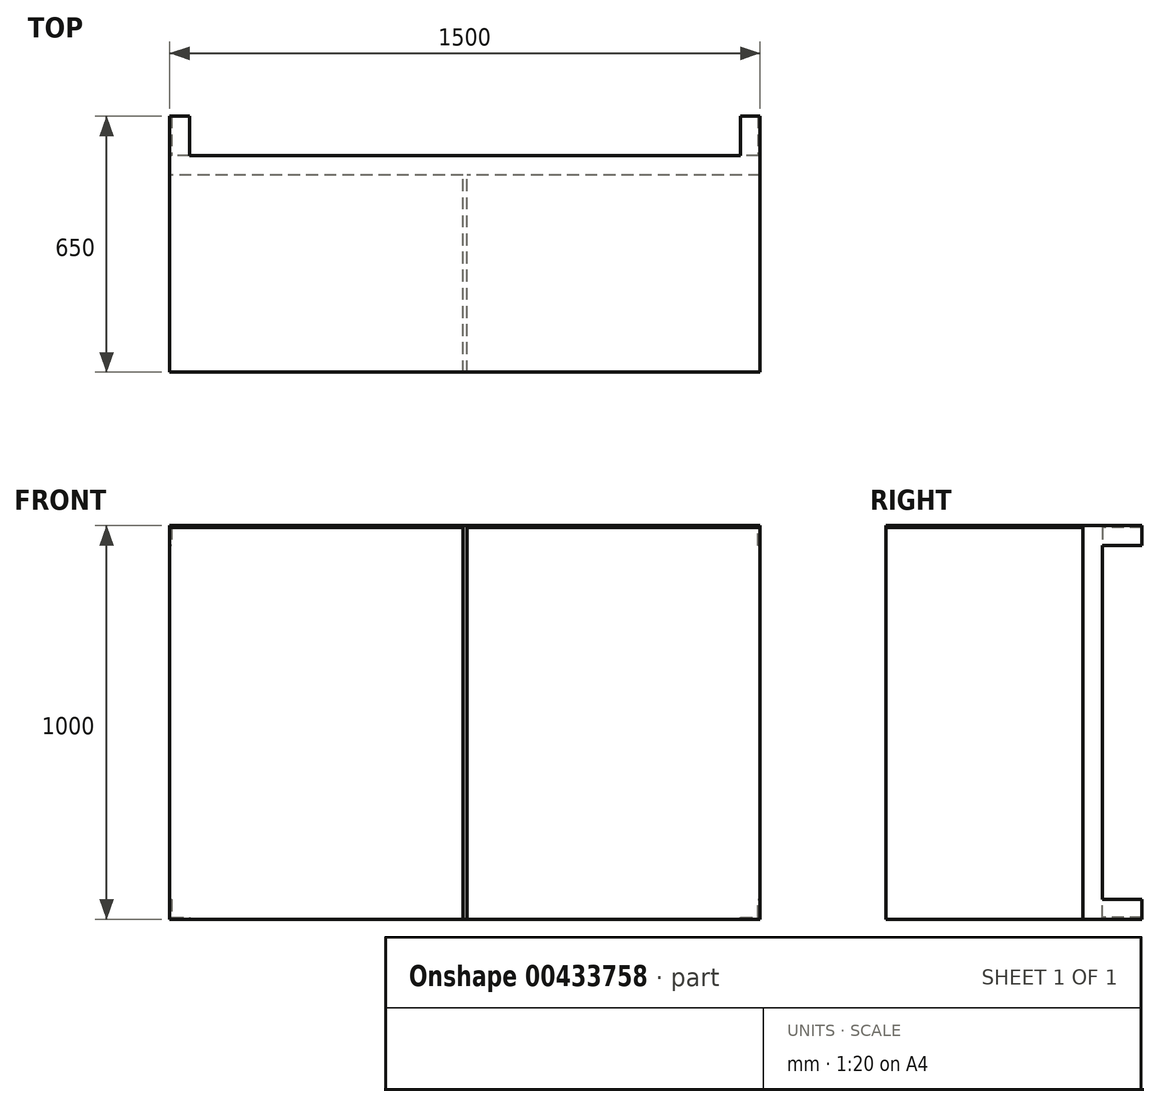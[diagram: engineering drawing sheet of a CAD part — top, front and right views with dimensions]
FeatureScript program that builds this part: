
annotation { "Feature Type Name" : "Feature", "Feature Type Description" : "" }
export const myFeature = defineFeature(function(context is Context, id is Id, definition is map)
    precondition{}
    {
        {
            var Q0;
            Q0=qCreatedBy(makeId("Front.planeOp"),FACE);
            var sketch = newSketch(context, id + "F0", { "sketchPlane" : qUnion([Q0])});
            skLineSegment(sketch, "E0.bottom", {"start": v(750, -500) * mm, "end": v(-750, -500) * mm});
            skLineSegment(sketch, "E0.top", {"start": v(750, 500) * mm, "end": v(-750, 500) * mm});
            skLineSegment(sketch, "E0.left", {"start": v(750, -500) * mm, "end": v(750, 500) * mm});
            skLineSegment(sketch, "E0.right", {"start": v(-750, -500) * mm, "end": v(-750, 500) * mm});
            skPoint(sketch, "E0.middle", {"position": v(0, 0) * mm});
            skSolve(sketch);
        }
        {
            var Q0;
            Q0=makeQuery(id+"F0.imprint","IMPRINT",FACE,{"disambiguationData":[TD([[makeQuery(id+"F0.imprint","IMPRINT",EDGE,{"derivedFrom":sQuery(id+"F0.wireOp",EDGE,"E0.bottom")}),-1.0]])]});
            extrude(context, id + "F1", {"entities" : qUnion([Q0]), "endBound" : BoundingType.SYMMETRIC, "depth" : 50 * mm});
        }
        {
            var Q0;
            Q0=makeQuery(id+"F1.opExtrude","CAP_FACE",FACE,{"disambiguationData":[OSD([sQuery(id+"F0.wireOp",EDGE,"E0.bottom"),sQuery(id+"F0.wireOp",EDGE,"E0.top"),sQuery(id+"F0.wireOp",EDGE,"E0.left"),sQuery(id+"F0.wireOp",EDGE,"E0.right")])],"isStart":true});
            var sketch = newSketch(context, id + "F2", { "sketchPlane" : qUnion([Q0])});
            skLineSegment(sketch, "E1", {"start": v(750, -500) * mm, "end": v(750, -450) * mm});
            skLineSegment(sketch, "E2", {"start": v(750, -500) * mm, "end": v(700, -500) * mm});
            skLineSegment(sketch, "E3", {"start": v(750, -450) * mm, "end": v(745, -450) * mm});
            skLineSegment(sketch, "E4", {"start": v(745, -450) * mm, "end": v(745, -495) * mm});
            skLineSegment(sketch, "E5", {"start": v(745, -495) * mm, "end": v(700, -495) * mm});
            skLineSegment(sketch, "E6", {"start": v(700, -495) * mm, "end": v(700, -500) * mm});
            skLineSegment(sketch, "E7", {"start": v(-750, -500) * mm, "end": v(-700, -500) * mm});
            skLineSegment(sketch, "E8", {"start": v(-750, -500) * mm, "end": v(-750, -450) * mm});
            skLineSegment(sketch, "E9", {"start": v(-700, -500) * mm, "end": v(-700, -495) * mm});
            skLineSegment(sketch, "E10", {"start": v(-700, -495) * mm, "end": v(-745, -495) * mm});
            skLineSegment(sketch, "E11", {"start": v(-745, -495) * mm, "end": v(-745, -450) * mm});
            skLineSegment(sketch, "E12", {"start": v(-745, -450) * mm, "end": v(-750, -450) * mm});
            skLineSegment(sketch, "E13", {"start": v(-750, 500) * mm, "end": v(-750, 450) * mm});
            skLineSegment(sketch, "E14", {"start": v(-750, 500) * mm, "end": v(-700, 500) * mm});
            skLineSegment(sketch, "E15", {"start": v(-750, 450) * mm, "end": v(-745, 450) * mm});
            skLineSegment(sketch, "E16", {"start": v(-745, 450) * mm, "end": v(-745, 495) * mm});
            skLineSegment(sketch, "E17", {"start": v(-745, 495) * mm, "end": v(-700, 495) * mm});
            skLineSegment(sketch, "E18", {"start": v(-700, 495) * mm, "end": v(-700, 500) * mm});
            skLineSegment(sketch, "E19", {"start": v(750, 500) * mm, "end": v(700, 500) * mm});
            skLineSegment(sketch, "E20", {"start": v(750, 500) * mm, "end": v(750, 450) * mm});
            skLineSegment(sketch, "E21", {"start": v(700, 500) * mm, "end": v(700, 495) * mm});
            skLineSegment(sketch, "E22", {"start": v(700, 495) * mm, "end": v(745, 495) * mm});
            skLineSegment(sketch, "E23", {"start": v(745, 495) * mm, "end": v(745, 450) * mm});
            skLineSegment(sketch, "E24", {"start": v(745, 450) * mm, "end": v(750, 450) * mm});
            skSolve(sketch);
        }
        {
            var Q0;
            Q0=makeQuery(id+"F2.imprint","IMPRINT",FACE,{"disambiguationData":[TD([[makeQuery(id+"F2.imprint","IMPRINT",EDGE,{"derivedFrom":sQuery(id+"F2.wireOp",EDGE,"E1")}),1.0]])]});
            var Q1;
            Q1=makeQuery(id+"F2.imprint","IMPRINT",FACE,{"disambiguationData":[TD([[makeQuery(id+"F2.imprint","IMPRINT",EDGE,{"derivedFrom":sQuery(id+"F2.wireOp",EDGE,"E7")}),1.0]])]});
            var Q2;
            Q2=makeQuery(id+"F2.imprint","IMPRINT",FACE,{"disambiguationData":[TD([[makeQuery(id+"F2.imprint","IMPRINT",EDGE,{"derivedFrom":sQuery(id+"F2.wireOp",EDGE,"E13")}),-1.0]])]});
            var Q3;
            Q3=makeQuery(id+"F2.imprint","IMPRINT",FACE,{"disambiguationData":[TD([[makeQuery(id+"F2.imprint","IMPRINT",EDGE,{"derivedFrom":sQuery(id+"F2.wireOp",EDGE,"E19")}),-1.0]])]});
            extrude(context, id + "F3", {"entities" : qUnion([Q0, Q1, Q2, Q3]), "operationType" : NewBodyOperationType.ADD, "depth" : 100 * mm});
        }
        {
            var Q0;
            Q0=makeQuery(id+"F1.opExtrude","CAP_FACE",FACE,{"disambiguationData":[OSD([sQuery(id+"F0.wireOp",EDGE,"E0.bottom"),sQuery(id+"F0.wireOp",EDGE,"E0.top"),sQuery(id+"F0.wireOp",EDGE,"E0.left"),sQuery(id+"F0.wireOp",EDGE,"E0.right")])],"isStart":false});
            var sketch = newSketch(context, id + "F4", { "sketchPlane" : qUnion([Q0])});
            skLineSegment(sketch, "E25.bottom", {"start": v(750, 500) * mm, "end": v(-750, 500) * mm});
            skLineSegment(sketch, "E25.top", {"start": v(750, 495) * mm, "end": v(-750, 495) * mm});
            skLineSegment(sketch, "E25.left", {"start": v(750, 500) * mm, "end": v(750, 495) * mm});
            skLineSegment(sketch, "E25.right", {"start": v(-750, 500) * mm, "end": v(-750, 495) * mm});
            skSolve(sketch);
        }
        {
            var Q0;
            Q0=makeQuery(id+"F4.imprint","IMPRINT",FACE,{"disambiguationData":[TD([[makeQuery(id+"F4.imprint","IMPRINT",EDGE,{"derivedFrom":sQuery(id+"F4.wireOp",EDGE,"E25.bottom")}),1.0]])]});
            extrude(context, id + "F5", {"entities" : qUnion([Q0]), "operationType" : NewBodyOperationType.ADD, "depth" : 500 * mm});
        }
        {
            var Q0;
            Q0=makeQuery(id+"F1.opExtrude","CAP_FACE",FACE,{"disambiguationData":[OSD([sQuery(id+"F0.wireOp",EDGE,"E0.bottom"),sQuery(id+"F0.wireOp",EDGE,"E0.top"),sQuery(id+"F0.wireOp",EDGE,"E0.left"),sQuery(id+"F0.wireOp",EDGE,"E0.right")])],"isStart":false});
            var sketch = newSketch(context, id + "F6", { "sketchPlane" : qUnion([Q0])});
            skLineSegment(sketch, "E26.bottom", {"start": v(0, -500) * mm, "end": v(5, -500) * mm});
            skLineSegment(sketch, "E26.top", {"start": v(0, 495) * mm, "end": v(5, 495) * mm});
            skLineSegment(sketch, "E26.right", {"start": v(5, -500) * mm, "end": v(5, 495) * mm});
            skLineSegment(sketch, "E27.MirrorCS", {"start": v(-5, -500) * mm, "end": v(-5, 495) * mm});
            skLineSegment(sketch, "E28", {"start": v(-5, -500) * mm, "end": v(0, -500) * mm});
            skLineSegment(sketch, "E29", {"start": v(-5, 495) * mm, "end": v(0, 495) * mm});
            skSolve(sketch);
        }
        {
            var Q0;
            Q0=makeQuery(id+"F6.imprint","IMPRINT",FACE,{"disambiguationData":[TD([[makeQuery(id+"F6.imprint","IMPRINT",EDGE,{"derivedFrom":sQuery(id+"F6.wireOp",EDGE,"E26.bottom")}),-1.0]])]});
            extrude(context, id + "F7", {"entities" : qUnion([Q0]), "operationType" : NewBodyOperationType.ADD, "depth" : 500 * mm});
        }
    });
